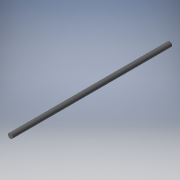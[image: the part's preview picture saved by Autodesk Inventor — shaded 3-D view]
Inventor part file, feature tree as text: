
AUTODESK INVENTOR PART (.ipt)
format: ipt  version: 2018 (Build 220112000, 112)  size: 93,696 bytes
history: native  units: mm
features: extrude x1, thread x1, sketch x1
ambient origin geometry x8: Origin, YZ Plane, XZ Plane, XY Plane, X Axis, Y Axis, Z Axis, Center Point
bodies: Solid1 (feature_tree)
feature tree (3):
  extrude  "Extrusion1"  Depth=100.0mm TaperAngle=0.0deg
  thread  "Thread1"  [1 undecoded]
  sketch  "Sketch1"  dims[d0=3.0mm d1=100.0mm d2=0.0mm d3=10.0mm d4=0.0mm]
note: 1 required parameter value undecoded (feature->parameter linkage not recoverable at this tier; creation-order binding heuristic only, values carry confidence <= 0.55)
